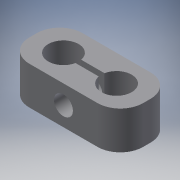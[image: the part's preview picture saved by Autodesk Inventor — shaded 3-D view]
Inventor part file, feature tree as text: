
AUTODESK INVENTOR PART (.ipt)
format: ipt  version: 2016 (Build 200138000, 138)  size: 131,072 bytes
history: native  units: mm
features: extrude x3, sketch x3, fillet x1
ambient origin geometry x8: Origin, YZ Plane, XZ Plane, XY Plane, X Axis, Y Axis, Z Axis, Center Point
bodies: Solid1 (feature_tree)
feature tree (7):
  extrude  "Extrusion1"  Depth=14.0mm
  extrude  "Extrusion2"  Depth=14.0mm
  fillet  "Fillet1"  Radius=10.0mm
  extrude  "Extrusion3"  Depth=30.0mm TaperAngle=0.0deg
  sketch  "Sketch1"  dims[d0=8.0mm d1=14.0mm]
  sketch  "Sketch2"  dims[d2=8.0mm d3=14.0mm d4=10.0mm d5=0.0mm]
  sketch  "Sketch3"  dims[d6=5.0mm d7=8.0mm d8=0.0mm d9=6.0mm d10=1.5mm d11=8.0mm d12=0.0mm d13=30.0mm]
